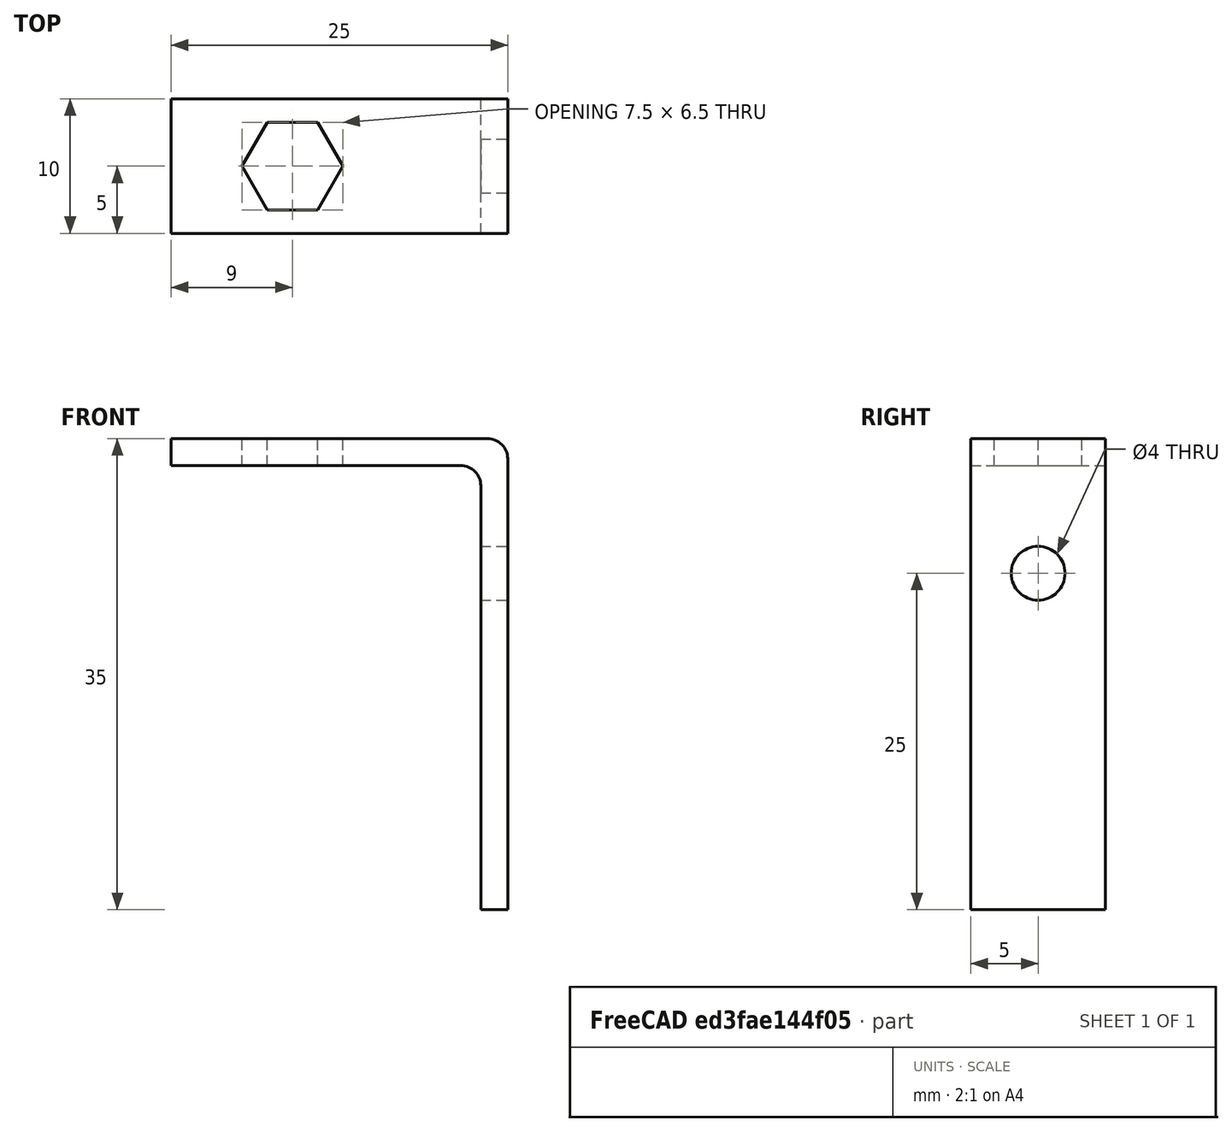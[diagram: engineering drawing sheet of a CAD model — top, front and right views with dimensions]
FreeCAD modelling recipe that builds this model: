
FCSTD DOCUMENT  (FreeCAD 0.17R13541 (Git))
Label: soporteSensorIR2
License: All rights reserved
LicenseURL: http://en.wikipedia.org/wiki/All_rights_reserved
objects: Part::Cut×5, Part::Cylinder×4, Part::MultiFuse×2, Part::Box×2, Part::Prism×2, Part::Fillet×1, Part::Feature×1, Mesh::Feature×1
note: 17 computed .brp shape members not serialized (recipe doc carries the construction recipe); baked Part::Feature solids carry a one-line shape summary decoded from their .brp

FEATURE [Part::Cylinder] Cylinder045  label="Cilindro045"
  Angle = 360
  AttacherType = Attacher::AttachEngine3D
  Height = 10
  Placement = pos=(22,5,-3) rot=(0,0,1;0rad)
  Radius = 2
FEATURE [Part::Cylinder] Cylinder047  label="Cilindro047"
  Angle = 360
  AttacherType = Attacher::AttachEngine3D
  Height = 10
  Placement = pos=(-14,7.5,29) rot=(0,0,1;0rad)
  Radius = 2
FEATURE [Part::MultiFuse] Fusion021
  Placement = pos=(0,-2.5,0) rot=(0,0,1;0rad)
  Shapes = -> [Cylinder045,Cylinder047]
FEATURE [Part::Cylinder] Cylinder046  label="Cilindro046"
  Angle = 360
  AttacherType = Attacher::AttachEngine3D
  Height = 10
  Placement = pos=(-2,5,25) rot=(0,1,0;1.5708rad)
  Radius = 2
FEATURE [Part::Box] Box027  label="Cubo025"
  AttacherType = Attacher::AttachEngine3D
  Height = 35
  Length = 2
  Width = 10
FEATURE [Part::Prism] Prism016  label="Prisma016"
  AttacherType = Attacher::AttachEngine3D
  Circumradius = 2.1
  Height = 10
  Placement = pos=(107,-15,4) rot=(0,0,1;0rad)
  Polygon = 6
FEATURE [Part::Prism] Prism017  label="Prisma017"
  AttacherType = Attacher::AttachEngine3D
  Circumradius = 3.75
  Height = 20
  Polygon = 6
FEATURE [Part::Box] Box028  label="Cubo026"
  AttacherType = Attacher::AttachEngine3D
  Height = 2
  Length = 25
  Placement = pos=(-23,0,33) rot=(0,0,1;0rad)
  Width = 10
FEATURE [Part::MultiFuse] Fusion020
  Shapes = -> [Box028,Box027]
FEATURE [Part::Cut] Cut038
  Base = -> Fusion020
  Tool = -> Fusion021
FEATURE [Part::Cut] Cut037
  Base = -> Cut038
  Placement = pos=(121,-20,-29) rot=(0,0,1;0rad)
  Tool = -> Cylinder046
FEATURE [Part::Cut] Cut039
  Base = -> Cut037
  Tool = -> Prism016
FEATURE [Part::Cylinder] Cylinder048  label="Cilindro048"
  Angle = 360
  AttacherType = Attacher::AttachEngine3D
  Height = 30
  Placement = pos=(0,0,-2) rot=(0,0,1;0rad)
  Radius = 2
FEATURE [Part::Cut] Cut040  label="separador015"
  Base = -> Prism017
  Placement = pos=(107,-15,4) rot=(0,0,1;0rad)
  Tool = -> Cylinder048
FEATURE [Part::Cut] Cut041
  Base = -> Cut039
  Tool = -> Cut040
FEATURE [Part::Fillet] Fillet010  label="soporteIR2"
  Base = -> Cut041
  Edges = 2 edges r=1.5: [Edge18,Edge29]
FEATURE [Part::Feature] Fillet010_solid  label="soporteIR2 (Solid)"
  shape: bbox 25 x 10 x 35 mm, 23 faces (baked)
FEATURE [Mesh::Feature] Mesh  label="soporteIR2 (Solid) (Meshed)"
